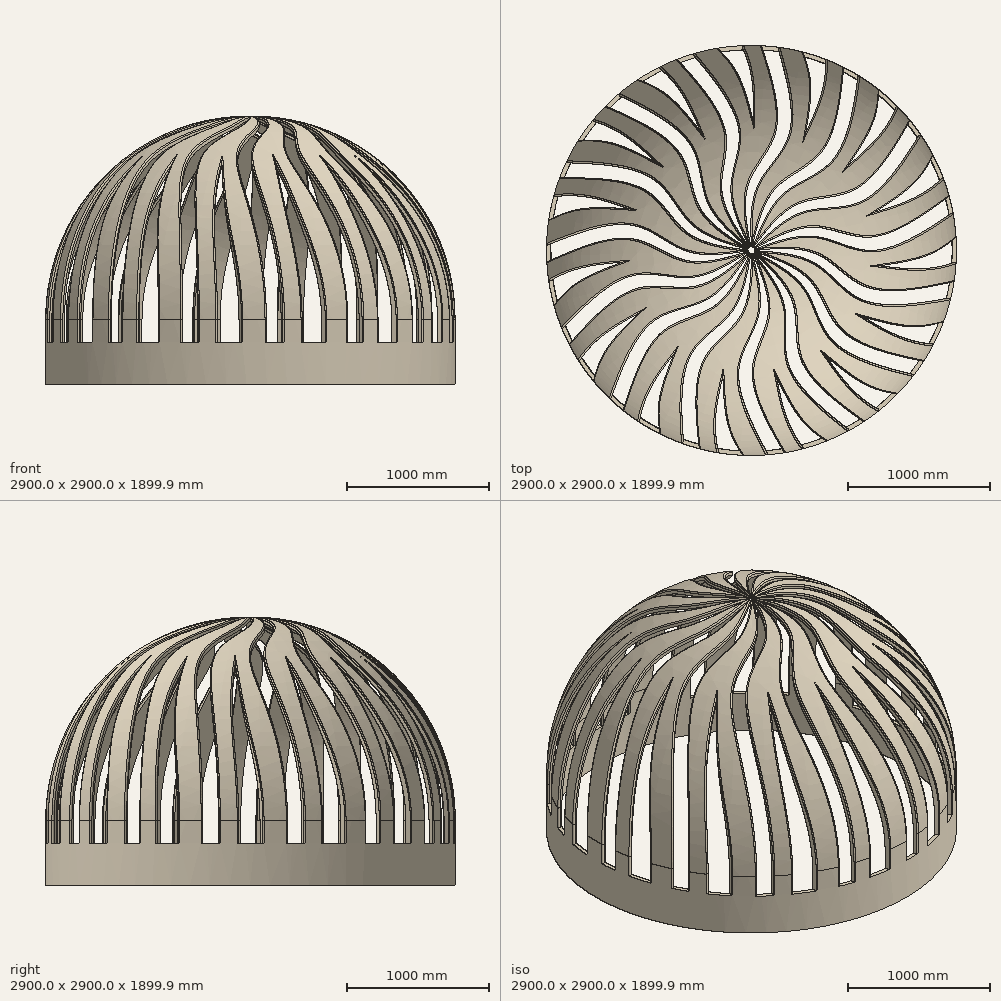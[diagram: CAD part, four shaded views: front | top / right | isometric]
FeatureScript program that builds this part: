
annotation { "Feature Type Name" : "Feature", "Feature Type Description" : "" }
export const myFeature = defineFeature(function(context is Context, id is Id, definition is map)
    precondition{}
    {
        {
            var Q0;
            Q0=qCreatedBy(makeId("Top.planeOp"),FACE);
            var sketch = newSketch(context, id + "F0", { "sketchPlane" : qUnion([Q0])});
            skCircle(sketch, "E0", {"center": v(0, 0) * mm, "radius": 1450 * mm});
            skSolve(sketch);
        }
        {
            var Q0;
            Q0=makeQuery(id+"F0.imprint","IMPRINT",FACE,{"disambiguationData":[TD([[makeQuery(id+"F0.imprint","IMPRINT",EDGE,{"derivedFrom":sQuery(id+"F0.wireOp",EDGE,"E0")}),1.0]])]});
            extrude(context, id + "F1", {"entities" : qUnion([Q0]), "depth" : 1900 * mm, "offsetDistance" : 25 * mm});
        }
        {
            var Q0;
            Q0=makeQuery(id+"F1.opExtrude","CAP_FACE",FACE,{"disambiguationData":[OSD([sQuery(id+"F0.wireOp",EDGE,"E0")])],"isStart":false});
            fillet(context, id + "F2", {"entities" : qUnion([Q0]), "radius" : 1440 * mm, "tangentPropagation" : true, "allowEdgeOverflow" : false});
        }
        {
            var Q0;
            Q0=makeQuery(id+"F1.opExtrude","CAP_FACE",FACE,{"disambiguationData":[OSD([sQuery(id+"F0.wireOp",EDGE,"E0")])],"isStart":true});
            shell(context, id + "F3", {"entities" : qUnion([Q0]), "thickness" : 30 * mm});
        }
        {
            var Q0;
            Q0=makeQuery(id+"F1.opExtrude","CAP_FACE",FACE,{"disambiguationData":[OSD([sQuery(id+"F0.wireOp",EDGE,"E0")])],"isStart":false});
            var sketch = newSketch(context, id + "F4", { "sketchPlane" : qUnion([Q0])});
            skLineSegment(sketch, "E1", {"start": v(0, 0) * mm, "end": v(0, 0) * mm});
            skFitSpline(sketch, "E2", {"points": [v(0, 0) * mm, v(443.42, 164.47) * mm, v(843.7, 94.34) * mm, v(1455.44, 423.4) * mm], "startDerivative": vector(1720.93, 881.17) * mm, "endDerivative": vector(1641.37, 1335.09) * mm, "construction": true});
            skLineSegment(sketch, "E3", {"start": v(1455.44, 423.4) * mm, "end": v(1493.38, 315.81) * mm, "construction": true});
            skPoint(sketch, "E4.2.0", {"position": v(338.19, 330.6) * mm});
            skPoint(sketch, "E4.2.1", {"position": v(374.7, 275.35) * mm});
            skPoint(sketch, "E4.2.2", {"position": v(778.83, 346.76) * mm});
            skPoint(sketch, "E4.2.3", {"position": v(732.39, 429.34) * mm});
            skPoint(sketch, "E4.2.4", {"position": v(1157.4, 978.78) * mm});
            skPoint(sketch, "E4.2.5", {"position": v(1235.82, 895.92) * mm});
            skPoint(sketch, "E4.4.0", {"position": v(174.48, 439.57) * mm});
            skPoint(sketch, "E4.4.1", {"position": v(230.3, 403.95) * mm});
            skPoint(sketch, "E4.4.2", {"position": v(570.46, 633.56) * mm});
            skPoint(sketch, "E4.4.3", {"position": v(494.44, 690.11) * mm});
            skPoint(sketch, "E4.4.4", {"position": v(659.23, 1364.92) * mm});
            skPoint(sketch, "E4.4.5", {"position": v(764.57, 1321.12) * mm});
            skPoint(sketch, "E4.6.0", {"position": v(-19.4, 472.54) * mm});
            skPoint(sketch, "E4.6.1", {"position": v(46.1, 462.7) * mm});
            skPoint(sketch, "E4.6.2", {"position": v(263.45, 810.8) * mm});
            skPoint(sketch, "E4.6.3", {"position": v(171, 831.56) * mm});
            skPoint(sketch, "E4.6.4", {"position": v(47.07, 1515.05) * mm});
            skPoint(sketch, "E4.6.5", {"position": v(161.12, 1517.88) * mm});
            skPoint(sketch, "E4.8.0", {"position": v(-209.91, 423.8) * mm});
            skPoint(sketch, "E4.8.1", {"position": v(-146.09, 441.44) * mm});
            skPoint(sketch, "E4.8.2", {"position": v(-89.11, 847.86) * mm});
            skPoint(sketch, "E4.8.3", {"position": v(-182, 829.21) * mm});
            skPoint(sketch, "E4.8.4", {"position": v(-573.22, 1403.21) * mm});
            skPoint(sketch, "E4.8.5", {"position": v(-470.18, 1452.19) * mm});
            skPoint(sketch, "E4.10.0", {"position": v(-364.14, 301.78) * mm});
            skPoint(sketch, "E4.10.1", {"position": v(-313, 343.86) * mm});
            skPoint(sketch, "E4.10.2", {"position": v(-426.27, 738.32) * mm});
            skPoint(sketch, "E4.10.3", {"position": v(-503.55, 683.5) * mm});
            skPoint(sketch, "E4.10.4", {"position": v(-1094.4, 1048.75) * mm});
            skPoint(sketch, "E4.10.5", {"position": v(-1020.19, 1135.4) * mm});
            skPoint(sketch, "E4.12.0", {"position": v(-455.4, 127.58) * mm});
            skPoint(sketch, "E4.12.1", {"position": v(-425.8, 186.82) * mm});
            skPoint(sketch, "E4.12.2", {"position": v(-689.71, 501.1) * mm});
            skPoint(sketch, "E4.12.3", {"position": v(-738.01, 419.6) * mm});
            skPoint(sketch, "E4.12.4", {"position": v(-1426.35, 512.95) * mm});
            skPoint(sketch, "E4.12.5", {"position": v(-1393.8, 622.29) * mm});
            skPoint(sketch, "E4.14.0", {"position": v(-467.92, -68.68) * mm});
            skPoint(sketch, "E4.14.1", {"position": v(-464.98, -2.53) * mm});
            skPoint(sketch, "E4.14.2", {"position": v(-833.9, 177.25) * mm});
            skPoint(sketch, "E4.14.3", {"position": v(-844.87, 83.14) * mm});
            skPoint(sketch, "E4.14.4", {"position": v(-1511.67, -111.55) * mm});
            skPoint(sketch, "E4.14.5", {"position": v(-1526.4, 1.58) * mm});
            skPoint(sketch, "E4.16.0", {"position": v(-399.53, -253.06) * mm});
            skPoint(sketch, "E4.16.1", {"position": v(-423.75, -191.43) * mm});
            skPoint(sketch, "E4.16.2", {"position": v(-833.9, -177.25) * mm});
            skPoint(sketch, "E4.16.3", {"position": v(-805.65, -267.69) * mm});
            skPoint(sketch, "E4.16.4", {"position": v(-1335.6, -716.76) * mm});
            skPoint(sketch, "E4.16.5", {"position": v(-1395.08, -619.4) * mm});
            skPoint(sketch, "E4.18.0", {"position": v(-262.06, -393.7) * mm});
            skPoint(sketch, "E4.18.1", {"position": v(-309.26, -347.24) * mm});
            skPoint(sketch, "E4.18.2", {"position": v(-689.71, -501.1) * mm});
            skPoint(sketch, "E4.18.3", {"position": v(-627.12, -572.23) * mm});
            skPoint(sketch, "E4.18.4", {"position": v(-928.6, -1198.03) * mm});
            skPoint(sketch, "E4.18.5", {"position": v(-1022.54, -1133.28) * mm});
            skPoint(sketch, "E4.20.0", {"position": v(-79.28, -466.24) * mm});
            skPoint(sketch, "E4.20.1", {"position": v(-141.28, -443) * mm});
            skPoint(sketch, "E4.20.2", {"position": v(-426.27, -738.32) * mm});
            skPoint(sketch, "E4.20.3", {"position": v(-340.15, -777.83) * mm});
            skPoint(sketch, "E4.20.4", {"position": v(-361.04, -1472.15) * mm});
            skPoint(sketch, "E4.20.5", {"position": v(-473.19, -1451.2) * mm});
            skPoint(sketch, "E4.22.0", {"position": v(117.22, -458.18) * mm});
            skPoint(sketch, "E4.22.1", {"position": v(51.12, -462.17) * mm});
            skPoint(sketch, "E4.22.2", {"position": v(-89.11, -847.86) * mm});
            skPoint(sketch, "E4.22.3", {"position": v(5.63, -848.94) * mm});
            skPoint(sketch, "E4.22.4", {"position": v(268.95, -1491.73) * mm});
            skPoint(sketch, "E4.22.5", {"position": v(157.98, -1518.2) * mm});
            skPoint(sketch, "E4.24.0", {"position": v(293.44, -370.9) * mm});
            skPoint(sketch, "E4.24.1", {"position": v(234.68, -401.42) * mm});
            skPoint(sketch, "E4.24.2", {"position": v(263.45, -810.8) * mm});
            skPoint(sketch, "E4.24.3", {"position": v(350.44, -773.25) * mm});
            skPoint(sketch, "E4.24.4", {"position": v(852.44, -1253.37) * mm});
            skPoint(sketch, "E4.24.5", {"position": v(761.83, -1322.7) * mm});
            skPoint(sketch, "E4.26.0", {"position": v(418.93, -219.48) * mm});
            skPoint(sketch, "E4.26.1", {"position": v(377.66, -271.27) * mm});
            skPoint(sketch, "E4.26.2", {"position": v(570.46, -633.56) * mm});
            skPoint(sketch, "E4.26.3", {"position": v(634.65, -563.87) * mm});
            skPoint(sketch, "E4.26.4", {"position": v(1288.53, -798.3) * mm});
            skPoint(sketch, "E4.26.5", {"position": v(1233.96, -898.48) * mm});
            skPoint(sketch, "E4.27.3", {"position": v(738.01, -419.6) * mm});
            skPoint(sketch, "E4.28.0", {"position": v(471.98, -30.1) * mm});
            skPoint(sketch, "E4.28.1", {"position": v(455.34, -94.2) * mm});
            skPoint(sketch, "E4.28.2", {"position": v(778.83, -346.76) * mm});
            skPoint(sketch, "E4.28.3", {"position": v(809.13, -256.98) * mm});
            skPoint(sketch, "E4.28.4", {"position": v(1501.83, -205.18) * mm});
            skPoint(sketch, "E4.28.5", {"position": v(1492.72, -318.9) * mm});
            skFitSpline(sketch, "E5", {"points": [v(0, 0) * mm, v(374.7, 275.35) * mm, v(778.83, 346.76) * mm, v(1235.82, 895.92) * mm], "startDerivative": vector(1131.7, 1116.14) * mm, "endDerivative": vector(1100.53, 1804.63) * mm});
            skFitSpline(sketch, "E6", {"points": [v(0, 0) * mm, v(338.19, 330.6) * mm, v(732.39, 429.34) * mm, v(1157.4, 978.78) * mm], "startDerivative": vector(974.1, 1303.77) * mm, "endDerivative": vector(1012.18, 1800.98) * mm});
            skFitSpline(sketch, "E7", {"points": [v(0, 0) * mm, v(230.3, 403.95) * mm, v(570.46, 633.56) * mm, v(764.57, 1321.12) * mm], "startDerivative": vector(579.9, 1479.95) * mm, "endDerivative": vector(271.37, 2096.24) * mm});
            skFitSpline(sketch, "E8", {"points": [v(0, 0) * mm, v(174.48, 439.57) * mm, v(494.44, 690.11) * mm, v(659.23, 1364.92) * mm], "startDerivative": vector(359.6, 1587.25) * mm, "endDerivative": vector(192.15, 2056.97) * mm});
            skFitSpline(sketch, "E9", {"points": [v(0, 0) * mm, v(46.1, 462.7) * mm, v(263.45, 810.8) * mm, v(161.12, 1517.88) * mm], "startDerivative": vector(-72.2, 1587.87) * mm, "endDerivative": vector(-604.7, 2025.39) * mm});
            skFitSpline(sketch, "E10", {"points": [v(0, 0) * mm, v(-19.4, 472.54) * mm, v(171, 831.56) * mm, v(47.07, 1515.05) * mm], "startDerivative": vector(-317.1, 1596.29) * mm, "endDerivative": vector(-661.1, 1957.29) * mm});
            skFitSpline(sketch, "E11", {"points": [v(0, 0) * mm, v(-146.09, 441.44) * mm, v(-89.11, 847.86) * mm, v(-470.18, 1452.19) * mm], "startDerivative": vector(-711.8, 1421.22) * mm, "endDerivative": vector(-1376.22, 1604.33) * mm});
            skFitSpline(sketch, "E12", {"points": [v(0, 0) * mm, v(-209.91, 423.8) * mm, v(-182, 829.21) * mm, v(-573.22, 1403.21) * mm], "startDerivative": vector(-938.95, 1329.3) * mm, "endDerivative": vector(-1400.05, 1519.18) * mm});
            skFitSpline(sketch, "E13", {"points": [v(0, 0) * mm, v(-313, 343.86) * mm, v(-426.27, 738.32) * mm, v(-1020.19, 1135.4) * mm], "startDerivative": vector(-1228.32, 1008.84) * mm, "endDerivative": vector(-1909.78, 905.86) * mm});
            skFitSpline(sketch, "E14", {"points": [v(0, 0) * mm, v(-364.14, 301.78) * mm, v(-503.55, 683.5) * mm, v(-1094.4, 1048.75) * mm], "startDerivative": vector(-1398.45, 832.48) * mm, "endDerivative": vector(-1896.92, 818.38) * mm});
            skFitSpline(sketch, "E15", {"points": [v(0, 0) * mm, v(-425.8, 186.82) * mm, v(-689.71, 501.1) * mm, v(-1393.8, 622.29) * mm], "startDerivative": vector(-1532.46, 422.02) * mm, "endDerivative": vector(-2113.12, 50.77) * mm});
            skFitSpline(sketch, "E16", {"points": [v(0, 0) * mm, v(-455.4, 127.58) * mm, v(-738.01, 419.6) * mm, v(-1426.35, 512.95) * mm], "startDerivative": vector(-1616.15, 191.7) * mm, "endDerivative": vector(-2065.79, -23.92) * mm});
            skFitSpline(sketch, "E17", {"points": [v(0, 0) * mm, v(-464.98, -2.53) * mm, v(-833.9, 177.25) * mm, v(-1526.4, 1.58) * mm], "startDerivative": vector(-1571.62, -237.77) * mm, "endDerivative": vector(-1951.08, -813.1) * mm});
            skFitSpline(sketch, "E18", {"points": [v(0, 0) * mm, v(-467.92, -68.68) * mm, v(-844.87, 83.14) * mm, v(-1511.67, -111.55) * mm], "startDerivative": vector(-1554.4, -482.21) * mm, "endDerivative": vector(-1877.46, -862.08) * mm});
            skFitSpline(sketch, "E19", {"points": [v(0, 0) * mm, v(-423.75, -191.43) * mm, v(-833.9, -177.25) * mm, v(-1395.08, -619.4) * mm], "startDerivative": vector(-1339.04, -856.45) * mm, "endDerivative": vector(-1451.68, -1536.38) * mm});
            skFitSpline(sketch, "E20", {"points": [v(0, 0) * mm, v(-399.53, -253.06) * mm, v(-805.65, -267.69) * mm, v(-1335.6, -716.76) * mm], "startDerivative": vector(-1223.88, -1072.75) * mm, "endDerivative": vector(-1364.5, -1551.18) * mm});
            skFitSpline(sketch, "E21", {"points": [v(0, 0) * mm, v(-309.26, -347.24) * mm, v(-689.71, -501.1) * mm, v(-1022.54, -1133.28) * mm], "startDerivative": vector(-874.92, -1327.04) * mm, "endDerivative": vector(-701.28, -1994) * mm});
            skFitSpline(sketch, "E22", {"points": [v(0, 0) * mm, v(-262.06, -393.7) * mm, v(-627.12, -572.23) * mm, v(-928.6, -1198.03) * mm], "startDerivative": vector(-681.74, -1477.8) * mm, "endDerivative": vector(-615.62, -1972.07) * mm});
            skFitSpline(sketch, "E23", {"points": [v(0, 0) * mm, v(-141.28, -443) * mm, v(-426.27, -738.32) * mm, v(-473.19, -1451.2) * mm], "startDerivative": vector(-259.52, -1568.18) * mm, "endDerivative": vector(170.39, -2106.85) * mm});
            skFitSpline(sketch, "E24", {"points": [v(0, 0) * mm, v(-79.28, -466.24) * mm, v(-340.15, -777.83) * mm, v(-361.04, -1472.15) * mm], "startDerivative": vector(-21.73, -1627.33) * mm, "endDerivative": vector(239.72, -2051.97) * mm});
            skFitSpline(sketch, "E25", {"points": [v(0, 0) * mm, v(51.12, -462.17) * mm, v(-89.11, -847.86) * mm, v(157.98, -1518.2) * mm], "startDerivative": vector(400.75, -1538.16) * mm, "endDerivative": vector(1012.6, -1855.4) * mm});
            skFitSpline(sketch, "E26", {"points": [v(0, 0) * mm, v(117.22, -458.18) * mm, v(5.63, -848.94) * mm, v(268.95, -1491.73) * mm], "startDerivative": vector(642.05, -1495.48) * mm, "endDerivative": vector(1053.6, -1777.07) * mm});
            skFitSpline(sketch, "E27", {"points": [v(0, 0) * mm, v(234.68, -401.42) * mm, v(263.45, -810.8) * mm, v(761.83, -1322.7) * mm], "startDerivative": vector(991.73, -1242.18) * mm, "endDerivative": vector(1679.7, -1283.13) * mm});
            skFitSpline(sketch, "E28", {"points": [v(0, 0) * mm, v(293.44, -370.9) * mm, v(350.44, -773.25) * mm, v(852.44, -1253.37) * mm], "startDerivative": vector(1194.8, -1105.04) * mm, "endDerivative": vector(1685.31, -1194.9) * mm});
            skFitSpline(sketch, "E29", {"points": [v(0, 0) * mm, v(377.66, -271.27) * mm, v(570.46, -633.56) * mm, v(1233.96, -898.48) * mm], "startDerivative": vector(1411.23, -731.41) * mm, "endDerivative": vector(2056.39, -489) * mm});
            skFitSpline(sketch, "E30", {"points": [v(0, 0) * mm, v(418.93, -219.48) * mm, v(634.65, -563.87) * mm, v(1288.53, -798.3) * mm], "startDerivative": vector(1540.97, -523.54) * mm, "endDerivative": vector(2025.62, -406.1) * mm});
            skFitSpline(sketch, "E31", {"points": [v(0, 0) * mm, v(455.34, -94.2) * mm, v(778.83, -346.76) * mm, v(1492.72, -318.9) * mm], "startDerivative": vector(1586.71, -94.18) * mm, "endDerivative": vector(2077.5, 389.68) * mm});
            skFitSpline(sketch, "E32", {"points": [v(-4.96, -0.45) * mm, v(471.98, -30.1) * mm, v(809.13, -256.98) * mm, v(1501.83, -205.18) * mm], "startDerivative": vector(1626.2, 146.66) * mm, "endDerivative": vector(2017.33, 453.02) * mm});
            skFitSpline(sketch, "E33", {"points": [v(0, 0) * mm, v(454.3, 99.15) * mm, v(852.53, 0) * mm, v(1493.38, 315.81) * mm], "startDerivative": vector(1487.84, 559.34) * mm, "endDerivative": vector(1739.4, 1200.99) * mm});
            skFitSpline(sketch, "E34", {"points": [v(0, 0) * mm, v(443.42, 164.47) * mm, v(843.7, 94.34) * mm, v(1455.44, 423.4) * mm], "startDerivative": vector(1420.17, 794.85) * mm, "endDerivative": vector(1657.2, 1233.59) * mm});
            skLineSegment(sketch, "E35", {"start": v(1455.44, 423.4) * mm, "end": v(1493.38, 315.81) * mm});
            skLineSegment(sketch, "E36", {"start": v(1157.4, 978.78) * mm, "end": v(1235.82, 895.92) * mm});
            skLineSegment(sketch, "E37", {"start": v(659.23, 1364.92) * mm, "end": v(764.57, 1321.12) * mm});
            skLineSegment(sketch, "E38", {"start": v(47.07, 1515.05) * mm, "end": v(161.12, 1517.88) * mm});
            skLineSegment(sketch, "E39", {"start": v(-470.18, 1452.19) * mm, "end": v(-573.22, 1403.21) * mm});
            skLineSegment(sketch, "E40", {"start": v(-1020.19, 1135.4) * mm, "end": v(-1094.4, 1048.75) * mm});
            skLineSegment(sketch, "E41", {"start": v(-1393.8, 622.29) * mm, "end": v(-1426.35, 512.95) * mm});
            skLineSegment(sketch, "E42", {"start": v(-1526.4, 1.58) * mm, "end": v(-1511.67, -111.55) * mm});
            skLineSegment(sketch, "E43", {"start": v(-1395.08, -619.4) * mm, "end": v(-1335.6, -716.76) * mm});
            skLineSegment(sketch, "E44", {"start": v(-1022.54, -1133.28) * mm, "end": v(-928.6, -1198.03) * mm});
            skLineSegment(sketch, "E45", {"start": v(-473.19, -1451.2) * mm, "end": v(-361.04, -1472.15) * mm});
            skLineSegment(sketch, "E46", {"start": v(157.98, -1518.2) * mm, "end": v(268.95, -1491.73) * mm});
            skLineSegment(sketch, "E47", {"start": v(761.83, -1322.7) * mm, "end": v(852.44, -1253.37) * mm});
            skLineSegment(sketch, "E48", {"start": v(1233.96, -898.48) * mm, "end": v(1288.53, -798.3) * mm});
            skLineSegment(sketch, "E49", {"start": v(1492.72, -318.9) * mm, "end": v(1501.83, -205.18) * mm});
            skFitSpline(sketch, "E50.trimOffspring", {"points": [v(0, 0) * mm, v(454.3, 99.15) * mm, v(852.53, 0) * mm, v(1493.38, 315.81) * mm], "startDerivative": vector(1487.84, 559.34) * mm, "endDerivative": vector(1620.1, 1322.46) * mm, "construction": true});
            skArc(sketch, "E51", {"start": v(-4.86, 24.52) * mm, "mid": v(-8.1, 23.65) * mm, "end": v(-11.19, 22.36) * mm});
            skArc(sketch, "E52.trimOffspring", {"start": v(-21.47, 12.8) * mm, "mid": v(-23, 9.81) * mm, "end": v(-24.1, 6.65) * mm});
            skArc(sketch, "E53.trimOffspring", {"start": v(-23.88, -7.4) * mm, "mid": v(-22.68, -10.52) * mm, "end": v(-21.07, -13.46) * mm});
            skArc(sketch, "E54.trimOffspring", {"start": v(-10.48, -22.7) * mm, "mid": v(-7.35, -23.9) * mm, "end": v(-4.1, -24.66) * mm});
            skArc(sketch, "E55.trimOffspring", {"start": v(-0.35, -25) * mm, "mid": v(3, -24.82) * mm, "end": v(6.3, -24.2) * mm});
            skArc(sketch, "E56.trimOffspring", {"start": v(18.34, -16.98) * mm, "mid": v(20.45, -14.38) * mm, "end": v(22.2, -11.51) * mm});
            skArc(sketch, "E57.trimOffspring", {"start": v(14.97, 20.02) * mm, "mid": v(12.16, 21.84) * mm, "end": v(9.13, 23.27) * mm});
            skArc(sketch, "E58.trimOffspring", {"start": v(5.54, 24.38) * mm, "mid": v(2.22, 24.9) * mm, "end": v(-1.13, 24.97) * mm});
            skArc(sketch, "E59.trimOffspring", {"start": v(-18.8, -16.47) * mm, "mid": v(-16.44, -18.84) * mm, "end": v(-13.77, -20.87) * mm});
            skArc(sketch, "E60.trimOffspring", {"start": v(23.67, -8.05) * mm, "mid": v(24.53, -4.82) * mm, "end": v(24.96, -1.49) * mm});
            skArc(sketch, "E61.trimOffspring", {"start": v(24.9, 2.23) * mm, "mid": v(24.37, 5.56) * mm, "end": v(23.4, 8.79) * mm});
            skLineSegment(sketch, "E62", {"start": v(-24.82, 2.96) * mm, "end": v(-24.72, -3.73) * mm});
            skLineSegment(sketch, "E63", {"start": v(-19.31, 15.87) * mm, "end": v(-14.41, 20.43) * mm});
            skLineSegment(sketch, "E64", {"start": v(17.8, 17.55) * mm, "end": v(21.82, 12.2) * mm});
            skLineSegment(sketch, "E65", {"start": v(9.85, -22.98) * mm, "end": v(15.6, -19.54) * mm});
            skPoint(sketch, "E66", {"position": v(-1045.92, -732.82) * mm});
            skPoint(sketch, "E67", {"position": v(-1111.7, -657.77) * mm});
            skPoint(sketch, "E68", {"position": v(-798.67, -446.53) * mm});
            skPoint(sketch, "E69", {"position": v(-1251.53, -904.6) * mm});
            skPoint(sketch, "E70", {"position": v(-1137.02, -1011.3) * mm});
            skPoint(sketch, "E71.1.0", {"position": v(-548, -732.77) * mm});
            skPoint(sketch, "E71.1.1", {"position": v(-748.05, -1053.08) * mm});
            skPoint(sketch, "E71.1.2", {"position": v(-657.43, -1094.88) * mm});
            skPoint(sketch, "E71.1.3", {"position": v(-627.38, -1386.34) * mm});
            skPoint(sketch, "E71.1.4", {"position": v(-775.4, -1335.43) * mm});
            skPoint(sketch, "E71.2.0", {"position": v(-202.58, -892.31) * mm});
            skPoint(sketch, "E71.2.1", {"position": v(-255.06, -1266.3) * mm});
            skPoint(sketch, "E71.2.2", {"position": v(-155.27, -1267.62) * mm});
            skPoint(sketch, "E71.2.3", {"position": v(-9.27, -1521.66) * mm});
            skPoint(sketch, "E71.2.4", {"position": v(-165.2, -1535.36) * mm});
            skPoint(sketch, "E71.3.0", {"position": v(177.87, -897.57) * mm});
            skPoint(sketch, "E71.3.1", {"position": v(282.04, -1260.56) * mm});
            skPoint(sketch, "E71.3.2", {"position": v(373.74, -1221.19) * mm});
            skPoint(sketch, "E71.3.3", {"position": v(610.45, -1393.88) * mm});
            skPoint(sketch, "E71.3.4", {"position": v(473.58, -1469.81) * mm});
            skPoint(sketch, "E71.4.0", {"position": v(527.57, -747.62) * mm});
            skPoint(sketch, "E71.4.1", {"position": v(770.37, -1036.86) * mm});
            skPoint(sketch, "E71.4.2", {"position": v(838.13, -963.6) * mm});
            skPoint(sketch, "E71.4.3", {"position": v(1124.61, -1025.08) * mm});
            skPoint(sketch, "E71.4.4", {"position": v(1030.46, -1150.12) * mm});
            skPoint(sketch, "E71.5.0", {"position": v(786.04, -468.4) * mm});
            skPoint(sketch, "E71.5.1", {"position": v(1125.5, -633.88) * mm});
            skPoint(sketch, "E71.5.2", {"position": v(1157.6, -539.39) * mm});
            skPoint(sketch, "E71.5.3", {"position": v(1444.32, -479.03) * mm});
            skPoint(sketch, "E71.5.4", {"position": v(1409.17, -631.56) * mm});
            skPoint(sketch, "E71.6.0", {"position": v(908.6, -108.2) * mm});
            skPoint(sketch, "E71.6.1", {"position": v(1286.02, -121.3) * mm});
            skPoint(sketch, "E71.6.2", {"position": v(1276.91, -21.92) * mm});
            skPoint(sketch, "E71.6.3", {"position": v(1514.3, 149.84) * mm});
            skPoint(sketch, "E71.6.4", {"position": v(1544.22, -3.8) * mm});
            skPoint(sketch, "E71.7.0", {"position": v(874.06, 270.72) * mm});
            skPoint(sketch, "E71.7.1", {"position": v(1224.17, 412.26) * mm});
            skPoint(sketch, "E71.7.2", {"position": v(1175.43, 499.35) * mm});
            skPoint(sketch, "E71.7.3", {"position": v(1322.43, 752.8) * mm});
            skPoint(sketch, "E71.7.4", {"position": v(1412.26, 624.62) * mm});
            skPoint(sketch, "E71.8.0", {"position": v(688.38, 602.82) * mm});
            skPoint(sketch, "E71.8.1", {"position": v(950.65, 874.53) * mm});
            skPoint(sketch, "E71.8.2", {"position": v(870.7, 934.27) * mm});
            skPoint(sketch, "E71.8.3", {"position": v(901.9, 1225.6) * mm});
            skPoint(sketch, "E71.8.4", {"position": v(1036.1, 1145.04) * mm});
            skPoint(sketch, "E71.9.0", {"position": v(383.68, 830.7) * mm});
            skPoint(sketch, "E71.9.1", {"position": v(512.76, 1185.6) * mm});
            skPoint(sketch, "E71.9.2", {"position": v(415.43, 1207.64) * mm});
            skPoint(sketch, "E71.9.3", {"position": v(325.44, 1486.48) * mm});
            skPoint(sketch, "E71.9.4", {"position": v(480.8, 1467.46) * mm});
            skPoint(sketch, "E71.10.0", {"position": v(12.63, 914.93) * mm});
            skPoint(sketch, "E71.10.1", {"position": v(-13.8, 1291.65) * mm});
            skPoint(sketch, "E71.10.2", {"position": v(-111.68, 1272.2) * mm});
            skPoint(sketch, "E71.10.3", {"position": v(-307.3, 1490.34) * mm});
            skPoint(sketch, "E71.10.4", {"position": v(-157.64, 1536.16) * mm});
            skPoint(sketch, "E71.11.0", {"position": v(-360.6, 840.97) * mm});
            skPoint(sketch, "E71.11.1", {"position": v(-537.96, 1174.37) * mm});
            skPoint(sketch, "E71.11.2", {"position": v(-619.48, 1116.8) * mm});
            skPoint(sketch, "E71.11.3", {"position": v(-886.91, 1236.5) * mm});
            skPoint(sketch, "E71.11.4", {"position": v(-768.82, 1339.23) * mm});
            skPoint(sketch, "E71.12.0", {"position": v(-671.48, 621.6) * mm});
            skPoint(sketch, "E71.12.1", {"position": v(-969.11, 854.03) * mm});
            skPoint(sketch, "E71.12.2", {"position": v(-1020.16, 768.28) * mm});
            skPoint(sketch, "E71.12.3", {"position": v(-1313.16, 768.86) * mm});
            skPoint(sketch, "E71.12.4", {"position": v(-1247.07, 910.74) * mm});
            skPoint(sketch, "E71.13.0", {"position": v(-866.25, 294.74) * mm});
            skPoint(sketch, "E71.13.1", {"position": v(-1232.7, 386.02) * mm});
            skPoint(sketch, "E71.13.2", {"position": v(-1244.45, 286.92) * mm});
            skPoint(sketch, "E71.13.3", {"position": v(-1512.36, 168.27) * mm});
            skPoint(sketch, "E71.13.4", {"position": v(-1509.68, 324.78) * mm});
            skPoint(sketch, "E71.14.0", {"position": v(-911.24, -83.07) * mm});
            skPoint(sketch, "E71.14.1", {"position": v(-1283.13, -148.73) * mm});
            skPoint(sketch, "E71.14.2", {"position": v(-1253.56, -244.05) * mm});
            skPoint(sketch, "E71.14.4", {"position": v(-1511.26, -317.34) * mm});
            skFitSpline(sketch, "E72", {"points": [v(-1450.05, -461.4) * mm, v(-1253.56, -244.05) * mm, v(-911.24, -83.07) * mm], "startDerivative": vector(367.35, 502.17) * mm, "endDerivative": vector(703.13, 259.65) * mm});
            skFitSpline(sketch, "E73", {"points": [v(-1512.36, 168.27) * mm, v(-1244.45, 286.92) * mm, v(-866.25, 294.74) * mm], "startDerivative": vector(539.84, 309.34) * mm, "endDerivative": vector(747.95, -48.79) * mm});
            skFitSpline(sketch, "E74", {"points": [v(-866.25, 294.74) * mm, v(-1232.7, 386.02) * mm, v(-1509.68, 324.78) * mm, v(-1512.36, 168.27) * mm], "startDerivative": vector(-888.53, 310.2) * mm, "endDerivative": vector(164.14, -687.57) * mm});
            skFitSpline(sketch, "E75", {"points": [v(-1137.02, -1011.3) * mm, v(-1045.92, -732.82) * mm, v(-798.67, -446.53) * mm], "startDerivative": vector(131.34, 608.17) * mm, "endDerivative": vector(536.73, 523.19) * mm});
            skFitSpline(sketch, "E76", {"points": [v(-798.67, -446.53) * mm, v(-1111.7, -657.77) * mm, v(-1251.53, -904.6) * mm, v(-1137.02, -1011.3) * mm], "startDerivative": vector(-825.06, -452.75) * mm, "endDerivative": vector(620.8, -338.1) * mm});
            skFitSpline(sketch, "E77", {"points": [v(-911.24, -83.07) * mm, v(-1283.13, -148.73) * mm, v(-1511.26, -317.34) * mm, v(-1450.05, -461.4) * mm], "startDerivative": vector(-937.88, -78.02) * mm, "endDerivative": vector(429.61, -561.37) * mm});
            skFitSpline(sketch, "E78", {"points": [v(-1313.16, 768.86) * mm, v(-1020.16, 768.28) * mm, v(-671.48, 621.6) * mm], "startDerivative": vector(618.99, 63.02) * mm, "endDerivative": vector(663.44, -348.79) * mm});
            skFitSpline(sketch, "E79", {"points": [v(-671.48, 621.6) * mm, v(-969.11, 854.03) * mm, v(-1247.07, 910.74) * mm, v(-1313.16, 768.86) * mm], "startDerivative": vector(-685.55, 644.77) * mm, "endDerivative": vector(-129.7, -694.9) * mm});
            skFitSpline(sketch, "E80", {"points": [v(-886.91, 1236.5) * mm, v(-619.48, 1116.8) * mm, v(-360.6, 840.97) * mm], "startDerivative": vector(591.1, -194.2) * mm, "endDerivative": vector(464.22, -588.48) * mm});
            skFitSpline(sketch, "E81", {"points": [v(-360.6, 840.97) * mm, v(-537.96, 1174.37) * mm, v(-768.82, 1339.23) * mm, v(-886.91, 1236.5) * mm], "startDerivative": vector(-364.03, 867.86) * mm, "endDerivative": vector(-401.13, -582.06) * mm});
            skFitSpline(sketch, "E82", {"points": [v(-307.3, 1490.34) * mm, v(-111.68, 1272.2) * mm, v(12.63, 914.93) * mm], "startDerivative": vector(461.02, -417.83) * mm, "endDerivative": vector(184.73, -726.42) * mm});
            skFitSpline(sketch, "E83", {"points": [v(12.63, 914.93) * mm, v(-13.8, 1291.65) * mm, v(-157.64, 1536.16) * mm, v(-307.3, 1490.34) * mm], "startDerivative": vector(20.44, 940.9) * mm, "endDerivative": vector(-603.2, -368.58) * mm});
            skFitSpline(sketch, "E84", {"points": [v(325.44, 1486.48) * mm, v(415.43, 1207.64) * mm, v(383.68, 830.7) * mm], "startDerivative": vector(251.22, -569.22) * mm, "endDerivative": vector(-126.7, -738.75) * mm});
            skFitSpline(sketch, "E85", {"points": [v(383.68, 830.7) * mm, v(512.76, 1185.6) * mm, v(480.8, 1467.46) * mm, v(325.44, 1486.48) * mm], "startDerivative": vector(401.37, 851.24) * mm, "endDerivative": vector(-700.96, -91.37) * mm});
            skFitSpline(sketch, "E86", {"points": [v(901.9, 1225.6) * mm, v(870.7, 934.27) * mm, v(688.38, 602.82) * mm], "startDerivative": vector(-2.02, -622.19) * mm, "endDerivative": vector(-416.23, -623.35) * mm});
            skFitSpline(sketch, "E87", {"points": [v(688.38, 602.82) * mm, v(950.65, 874.53) * mm, v(1036.1, 1145.04) * mm, v(901.9, 1225.6) * mm], "startDerivative": vector(712.9, 614.4) * mm, "endDerivative": vector(-677.53, 201.64) * mm});
            skFitSpline(sketch, "E88", {"points": [v(1322.43, 752.8) * mm, v(1175.43, 499.35) * mm, v(874.06, 270.72) * mm], "startDerivative": vector(-254.92, -567.57) * mm, "endDerivative": vector(-633.78, -400.16) * mm});
            skFitSpline(sketch, "E89", {"points": [v(874.06, 270.72) * mm, v(1224.17, 412.26) * mm, v(1412.26, 624.62) * mm, v(1322.43, 752.8) * mm], "startDerivative": vector(901.16, 271.32) * mm, "endDerivative": vector(-536.94, 459.78) * mm});
            skFitSpline(sketch, "E90", {"points": [v(1514.3, 149.84) * mm, v(1276.91, -21.92) * mm, v(908.6, -108.2) * mm], "startDerivative": vector(-463.73, -414.82) * mm, "endDerivative": vector(-741.75, -107.79) * mm});
            skFitSpline(sketch, "E91", {"points": [v(908.6, -108.2) * mm, v(1286.02, -121.3) * mm, v(1544.22, -3.8) * mm, v(1514.3, 149.84) * mm], "startDerivative": vector(933.6, -118.68) * mm, "endDerivative": vector(-303.5, 638.42) * mm});
            skFitSpline(sketch, "E92", {"points": [v(1444.32, -479.03) * mm, v(1157.6, -539.39) * mm, v(786.04, -468.4) * mm], "startDerivative": vector(-592.36, -190.34) * mm, "endDerivative": vector(-721.46, 203.23) * mm});
            skFitSpline(sketch, "E93", {"points": [v(786.04, -468.4) * mm, v(1125.5, -633.88) * mm, v(1409.17, -631.56) * mm, v(1444.32, -479.03) * mm], "startDerivative": vector(804.62, -488.15) * mm, "endDerivative": vector(-17.6, 706.67) * mm});
            skFitSpline(sketch, "E94", {"points": [v(1124.61, -1025.08) * mm, v(838.13, -963.6) * mm, v(527.57, -747.62) * mm], "startDerivative": vector(-618.57, 67.05) * mm, "endDerivative": vector(-576.43, 479.1) * mm});
            skFitSpline(sketch, "E95", {"points": [v(527.57, -747.62) * mm, v(770.37, -1036.86) * mm, v(1030.46, -1150.12) * mm, v(1124.61, -1025.08) * mm], "startDerivative": vector(536.5, -773.21) * mm, "endDerivative": vector(271.35, 652.74) * mm});
            skFitSpline(sketch, "E96", {"points": [v(610.45, -1393.88) * mm, v(373.74, -1221.19) * mm, v(177.87, -897.57) * mm], "startDerivative": vector(-537.82, 312.85) * mm, "endDerivative": vector(-331.72, 672.14) * mm});
            skFitSpline(sketch, "E97", {"points": [v(177.87, -897.57) * mm, v(282.04, -1260.56) * mm, v(473.58, -1469.81) * mm, v(610.45, -1393.88) * mm], "startDerivative": vector(175.63, -924.58) * mm, "endDerivative": vector(513.38, 485.94) * mm});
            skFitSpline(sketch, "E98", {"points": [v(-9.27, -1521.66) * mm, v(-155.27, -1267.62) * mm, v(-202.58, -892.31) * mm], "startDerivative": vector(-364.07, 504.55) * mm, "endDerivative": vector(-29.66, 748.95) * mm});
            skFitSpline(sketch, "E99", {"points": [v(-202.58, -892.31) * mm, v(-255.06, -1266.3) * mm, v(-165.2, -1535.36) * mm, v(-9.27, -1521.66) * mm], "startDerivative": vector(-215.61, -916.09) * mm, "endDerivative": vector(666.65, 235.11) * mm});
            skFitSpline(sketch, "E100", {"points": [v(-627.38, -1386.34) * mm, v(-657.43, -1094.88) * mm, v(-548, -732.77) * mm], "startDerivative": vector(-127.38, 609.01) * mm, "endDerivative": vector(277.53, 696.27) * mm});
            skFitSpline(sketch, "E101", {"points": [v(-548, -732.77) * mm, v(-748.05, -1053.08) * mm, v(-775.4, -1335.43) * mm, v(-627.38, -1386.34) * mm], "startDerivative": vector(-569.58, -749.19) * mm, "endDerivative": vector(704.64, -56.36) * mm});
            skSolve(sketch);
        }
        {
            var Q0;
            Q0=qSketchRegion(id+"F4",true);
            extrude(context, id + "F5", {"entities" : qUnion([Q0]), "operationType" : NewBodyOperationType.REMOVE, "oppositeDirection" : true, "depth" : 1600 * mm, "offsetDistance" : 25 * mm});
        }
        {
            var Q0;
            {var subQ0=sQuery(id+"F0.wireOp",EDGE,"E0");Q0=makeQuery(id+"F5.boolean.opBoolean","SPLIT",FACE,{"disambiguationData":[TD([makeQuery(id+"F5.opExtrude","SWEPT_FACE",FACE,{"disambiguationData":[OSD([sQuery(id+"F4.wireOp",EDGE,"E26")])]})])],"derivedFrom":makeQuery(id+"F2.opFillet","BLEND_FACE",FACE,{"disambiguationData":[OSD([subQ0])]})});}
            var Q1;
            {var subQ0=sQuery(id+"F0.wireOp",EDGE,"E0");Q1=makeQuery(id+"F5.boolean.opBoolean","SPLIT",FACE,{"disambiguationData":[TD([makeQuery(id+"F5.opExtrude","SWEPT_FACE",FACE,{"disambiguationData":[OSD([sQuery(id+"F4.wireOp",EDGE,"E28")])]})])],"derivedFrom":makeQuery(id+"F2.opFillet","BLEND_FACE",FACE,{"disambiguationData":[OSD([subQ0])]})});}
            var Q2;
            {var subQ0=sQuery(id+"F0.wireOp",EDGE,"E0");Q2=makeQuery(id+"F5.boolean.opBoolean","SPLIT",FACE,{"disambiguationData":[TD([makeQuery(id+"F5.opExtrude","SWEPT_FACE",FACE,{"disambiguationData":[OSD([sQuery(id+"F4.wireOp",EDGE,"E30")])]})])],"derivedFrom":makeQuery(id+"F2.opFillet","BLEND_FACE",FACE,{"disambiguationData":[OSD([subQ0])]})});}
            var Q3;
            {var subQ0=sQuery(id+"F0.wireOp",EDGE,"E0");Q3=makeQuery(id+"F5.boolean.opBoolean","SPLIT",FACE,{"disambiguationData":[TD([makeQuery(id+"F5.opExtrude","SWEPT_FACE",FACE,{"disambiguationData":[OSD([sQuery(id+"F4.wireOp",EDGE,"E33")])]})])],"derivedFrom":makeQuery(id+"F2.opFillet","BLEND_FACE",FACE,{"disambiguationData":[OSD([subQ0])]})});}
            var Q4;
            {var subQ0=sQuery(id+"F0.wireOp",EDGE,"E0");Q4=makeQuery(id+"F5.boolean.opBoolean","SPLIT",FACE,{"disambiguationData":[TD([makeQuery(id+"F5.opExtrude","SWEPT_FACE",FACE,{"disambiguationData":[OSD([sQuery(id+"F4.wireOp",EDGE,"E5")])]})])],"derivedFrom":makeQuery(id+"F2.opFillet","BLEND_FACE",FACE,{"disambiguationData":[OSD([subQ0])]})});}
            var Q5;
            {var subQ0=sQuery(id+"F0.wireOp",EDGE,"E0");Q5=makeQuery(id+"F5.boolean.opBoolean","SPLIT",FACE,{"disambiguationData":[TD([makeQuery(id+"F5.opExtrude","SWEPT_FACE",FACE,{"disambiguationData":[OSD([sQuery(id+"F4.wireOp",EDGE,"E6")])]})])],"derivedFrom":makeQuery(id+"F2.opFillet","BLEND_FACE",FACE,{"disambiguationData":[OSD([subQ0])]})});}
            var Q6;
            {var subQ0=sQuery(id+"F0.wireOp",EDGE,"E0");Q6=makeQuery(id+"F5.boolean.opBoolean","SPLIT",FACE,{"disambiguationData":[TD([makeQuery(id+"F5.opExtrude","SWEPT_FACE",FACE,{"disambiguationData":[OSD([sQuery(id+"F4.wireOp",EDGE,"E8")])]})])],"derivedFrom":makeQuery(id+"F2.opFillet","BLEND_FACE",FACE,{"disambiguationData":[OSD([subQ0])]})});}
            var Q7;
            {var subQ0=sQuery(id+"F0.wireOp",EDGE,"E0");Q7=makeQuery(id+"F5.boolean.opBoolean","SPLIT",FACE,{"disambiguationData":[TD([makeQuery(id+"F5.opExtrude","SWEPT_FACE",FACE,{"disambiguationData":[OSD([sQuery(id+"F4.wireOp",EDGE,"E10")])]})])],"derivedFrom":makeQuery(id+"F2.opFillet","BLEND_FACE",FACE,{"disambiguationData":[OSD([subQ0])]})});}
            var Q8;
            {var subQ0=sQuery(id+"F0.wireOp",EDGE,"E0");Q8=makeQuery(id+"F5.boolean.opBoolean","SPLIT",FACE,{"disambiguationData":[TD([makeQuery(id+"F5.opExtrude","SWEPT_FACE",FACE,{"disambiguationData":[OSD([sQuery(id+"F4.wireOp",EDGE,"E12")])]})])],"derivedFrom":makeQuery(id+"F2.opFillet","BLEND_FACE",FACE,{"disambiguationData":[OSD([subQ0])]})});}
            var Q9;
            {var subQ0=sQuery(id+"F0.wireOp",EDGE,"E0");Q9=makeQuery(id+"F5.boolean.opBoolean","SPLIT",FACE,{"disambiguationData":[TD([makeQuery(id+"F5.opExtrude","SWEPT_FACE",FACE,{"disambiguationData":[OSD([sQuery(id+"F4.wireOp",EDGE,"E14")])]})])],"derivedFrom":makeQuery(id+"F2.opFillet","BLEND_FACE",FACE,{"disambiguationData":[OSD([subQ0])]})});}
            var Q10;
            {var subQ0=sQuery(id+"F0.wireOp",EDGE,"E0");Q10=makeQuery(id+"F5.boolean.opBoolean","SPLIT",FACE,{"disambiguationData":[TD([makeQuery(id+"F5.opExtrude","SWEPT_FACE",FACE,{"disambiguationData":[OSD([sQuery(id+"F4.wireOp",EDGE,"E16")])]})])],"derivedFrom":makeQuery(id+"F2.opFillet","BLEND_FACE",FACE,{"disambiguationData":[OSD([subQ0])]})});}
            var Q11;
            {var subQ0=sQuery(id+"F0.wireOp",EDGE,"E0");Q11=makeQuery(id+"F5.boolean.opBoolean","SPLIT",FACE,{"disambiguationData":[TD([makeQuery(id+"F5.opExtrude","SWEPT_FACE",FACE,{"disambiguationData":[OSD([sQuery(id+"F4.wireOp",EDGE,"E18")])]})])],"derivedFrom":makeQuery(id+"F2.opFillet","BLEND_FACE",FACE,{"disambiguationData":[OSD([subQ0])]})});}
            var Q12;
            {var subQ0=sQuery(id+"F0.wireOp",EDGE,"E0");Q12=makeQuery(id+"F5.boolean.opBoolean","SPLIT",FACE,{"disambiguationData":[TD([makeQuery(id+"F5.opExtrude","SWEPT_FACE",FACE,{"disambiguationData":[OSD([sQuery(id+"F4.wireOp",EDGE,"E20")])]})])],"derivedFrom":makeQuery(id+"F2.opFillet","BLEND_FACE",FACE,{"disambiguationData":[OSD([subQ0])]})});}
            var Q13;
            {var subQ0=sQuery(id+"F0.wireOp",EDGE,"E0");Q13=makeQuery(id+"F5.boolean.opBoolean","SPLIT",FACE,{"disambiguationData":[TD([makeQuery(id+"F5.opExtrude","SWEPT_FACE",FACE,{"disambiguationData":[OSD([sQuery(id+"F4.wireOp",EDGE,"E22")])]})])],"derivedFrom":makeQuery(id+"F2.opFillet","BLEND_FACE",FACE,{"disambiguationData":[OSD([subQ0])]})});}
            var Q14;
            {var subQ0=sQuery(id+"F0.wireOp",EDGE,"E0");Q14=makeQuery(id+"F5.boolean.opBoolean","SPLIT",FACE,{"disambiguationData":[TD([makeQuery(id+"F5.opExtrude","SWEPT_FACE",FACE,{"disambiguationData":[OSD([sQuery(id+"F4.wireOp",EDGE,"E24")])]})])],"derivedFrom":makeQuery(id+"F2.opFillet","BLEND_FACE",FACE,{"disambiguationData":[OSD([subQ0])]})});}
            fillet(context, id + "F6", {"entities" : qUnion([Q0, Q1, Q2, Q3, Q4, Q5, Q6, Q7, Q8, Q9, Q10, Q11, Q12, Q13, Q14]), "radius" : 10 * mm, "tangentPropagation" : true, "allowEdgeOverflow" : false});
        }
    });
